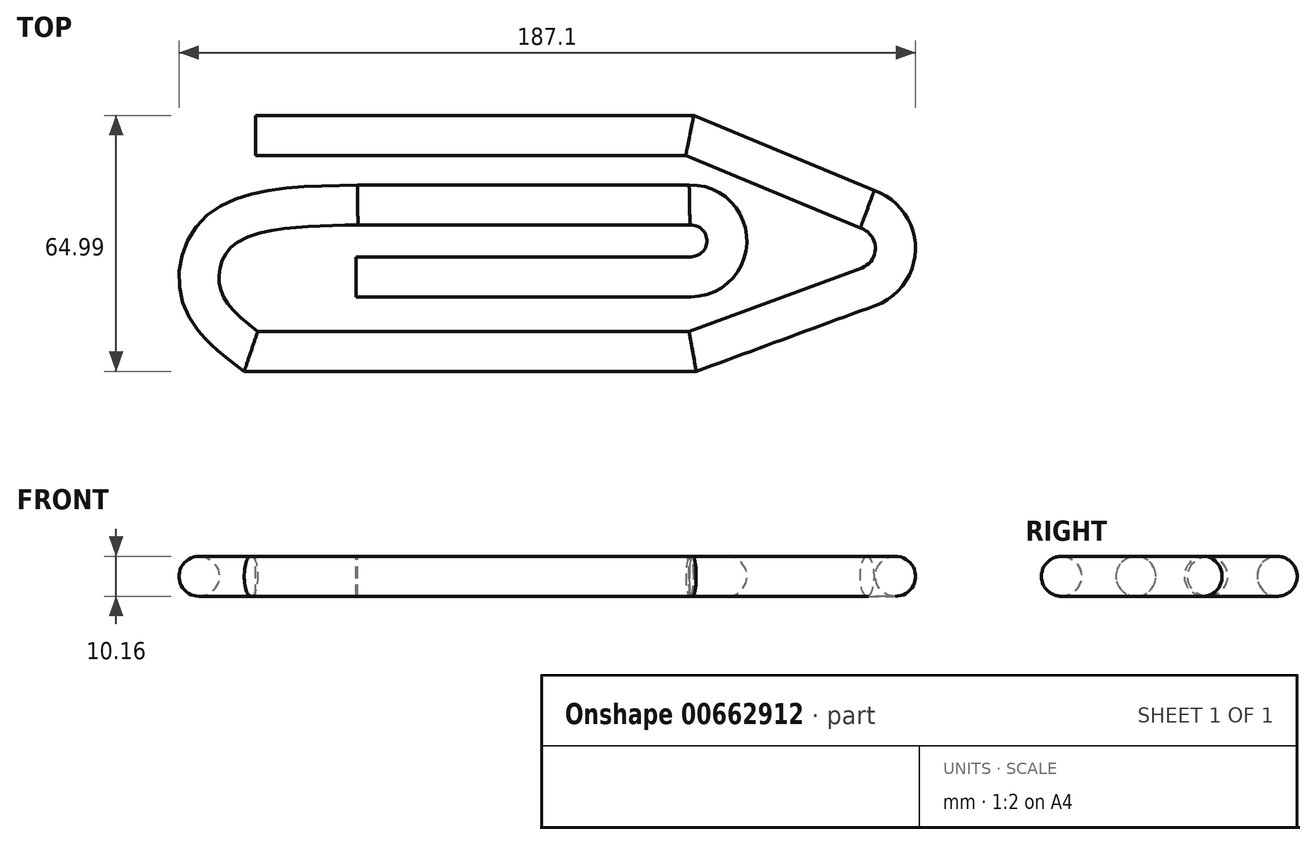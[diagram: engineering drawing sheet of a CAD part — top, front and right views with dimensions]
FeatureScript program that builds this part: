
annotation { "Feature Type Name" : "Feature", "Feature Type Description" : "" }
export const myFeature = defineFeature(function(context is Context, id is Id, definition is map)
    precondition{}
    {
        {
            var Q0;
            Q0=qCreatedBy(makeId("Top.planeOp"),FACE);
            var sketch = newSketch(context, id + "F0", { "sketchPlane" : qUnion([Q0])});
            skLineSegment(sketch, "E0", {"start": v(-117.2, 54.25) * mm, "end": v(-6.95, 54.25) * mm});
            skLineSegment(sketch, "E1", {"start": v(-6.95, 36.6) * mm, "end": v(-91.26, 36.6) * mm});
            skLineSegment(sketch, "E2", {"start": v(-91.62, 18.94) * mm, "end": v(-6.6, 18.94) * mm});
            skLineSegment(sketch, "E3", {"start": v(-6.23, 0) * mm, "end": v(-118.28, 0) * mm});
            skLineSegment(sketch, "E4", {"start": v(-6.95, 54.25) * mm, "end": v(38.08, 35.52) * mm});
            skLineSegment(sketch, "E5", {"start": v(-6.23, 0) * mm, "end": v(38.44, 16.42) * mm});
            skArc(sketch, "E6", {"start": v(38.44, 16.42) * mm, "mid": v(45.06, 26.1) * mm, "end": v(38.08, 35.52) * mm});
            skArc(sketch, "E7", {"start": v(-6.6, 18.94) * mm, "mid": v(2.24, 27.96) * mm, "end": v(-6.95, 36.6) * mm});
            skFitSpline(sketch, "E8", {"points": [v(-91.26, 36.6) * mm, v(-126.2, 30.11) * mm, v(-130.53, 13.54) * mm, v(-118.28, 0) * mm], "startDerivative": vector(-101.48, -1.69) * mm, "endDerivative": vector(52.45, -40.03) * mm});
            skSolve(sketch);
        }
        {
            var Q0;
            Q0=sQuery(id+"F0.wireOp",VERTEX,"E0.start");
            var Q1;
            Q1=sQuery(id+"F0.wireOp",EDGE,"E0");
            cPlane(context, id + "F1", {"entities" : qUnion([Q0, Q1]), "cplaneType" : CPlaneType.CURVE_POINT, "offset" : 25.4 * mm, "width" : 152.4 * mm, "height" : 152.4 * mm});
        }
        {
            var Q0;
            Q0=qCreatedBy(id+"F1.planeOp",FACE);
            var sketch = newSketch(context, id + "F2", { "sketchPlane" : qUnion([Q0])});
            skCircle(sketch, "E9", {"center": v(54.54, 0) * mm, "radius": 5.08 * mm});
            skSolve(sketch);
        }
        {
            var Q0;
            Q0=makeQuery(id+"F2.imprint","IMPRINT",FACE,{"disambiguationData":[TD([[makeQuery(id+"F2.imprint","IMPRINT",EDGE,{"derivedFrom":sQuery(id+"F2.wireOp",EDGE,"E9")}),1.0]])]});
            var Q1;
            Q1=sQuery(id+"F0.wireOp",EDGE,"E0");
            var Q2;
            Q2=sQuery(id+"F0.wireOp",EDGE,"E4");
            var Q3;
            Q3=sQuery(id+"F0.wireOp",EDGE,"E6");
            var Q4;
            Q4=sQuery(id+"F0.wireOp",EDGE,"E5");
            var Q5;
            Q5=sQuery(id+"F0.wireOp",EDGE,"E3");
            var Q6;
            Q6=sQuery(id+"F0.wireOp",EDGE,"E8");
            var Q7;
            Q7=sQuery(id+"F0.wireOp",EDGE,"E1");
            var Q8;
            Q8=sQuery(id+"F0.wireOp",EDGE,"E7");
            var Q9;
            Q9=sQuery(id+"F0.wireOp",EDGE,"E2");
            sweep(context, id + "F3", {"profiles" : qUnion([Q0]), "path" : qUnion([Q1, Q2, Q3, Q4, Q5, Q6, Q7, Q8, Q9])});
        }
    });
